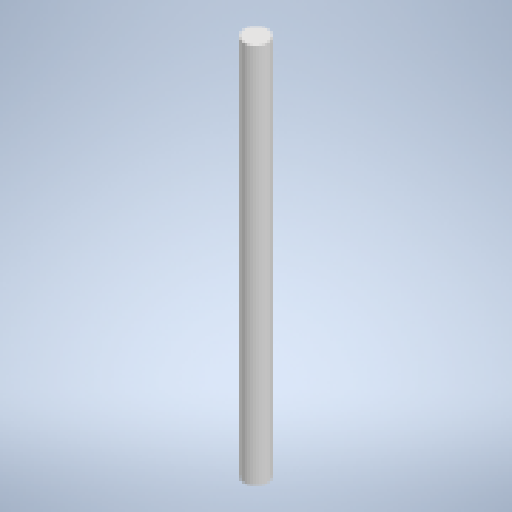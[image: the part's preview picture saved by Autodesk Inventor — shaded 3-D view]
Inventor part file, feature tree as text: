
AUTODESK INVENTOR PART (.ipt)
format: ipt  version: 2023 (Build 270158000, 158)  size: 229,888 bytes
history: native  units: mm
features: extrude x1, sketch x1
ambient origin geometry x8: Origin, YZ Plane, XZ Plane, XY Plane, X Axis, Y Axis, Z Axis, Center Point
bodies: Solid1 (feature_tree)
feature tree (2):
  extrude  "Extrusion1"  Depth=150.0mm TaperAngle=0.0deg
  sketch  "Sketch1"  dims[d0=9.36mm d1=150.0mm d2=0.0mm]
